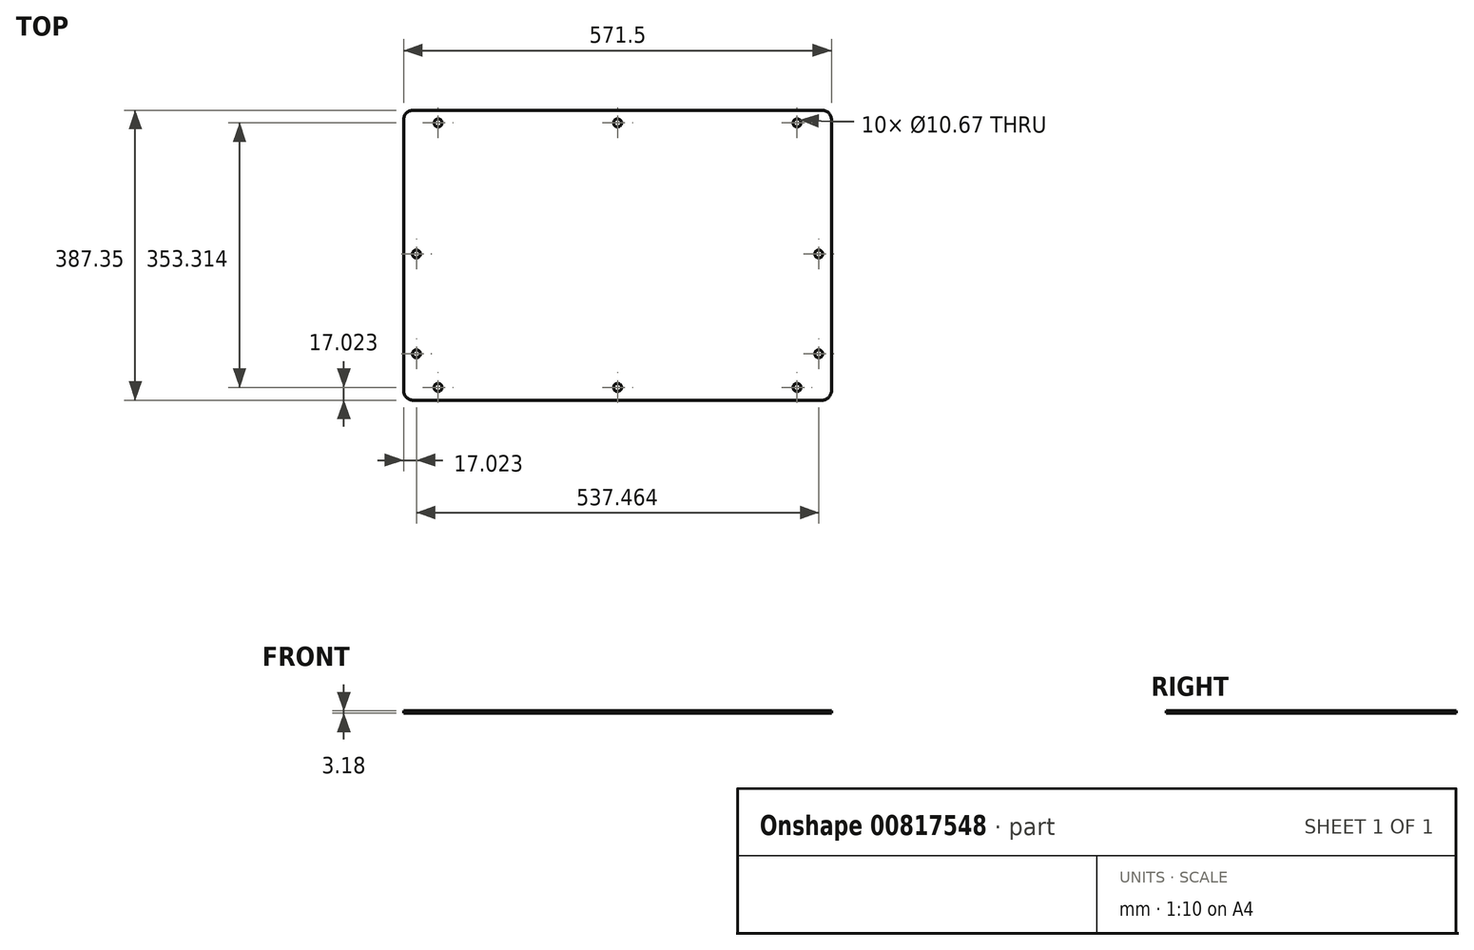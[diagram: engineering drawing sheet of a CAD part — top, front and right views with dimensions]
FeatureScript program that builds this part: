
annotation { "Feature Type Name" : "Feature", "Feature Type Description" : "" }
export const myFeature = defineFeature(function(context is Context, id is Id, definition is map)
    precondition{}
    {
        {
            var Q0;
            Q0=qCreatedBy(makeId("Top.planeOp"),FACE);
            var sketch = newSketch(context, id + "F0", { "sketchPlane" : qUnion([Q0])});
            skLineSegment(sketch, "E0.bottom", {"start": v(-512.78, 325.42) * mm, "end": v(33.32, 325.42) * mm});
            skLineSegment(sketch, "E0.top", {"start": v(-512.78, -61.93) * mm, "end": v(33.32, -61.93) * mm});
            skLineSegment(sketch, "E0.left", {"start": v(-525.48, 312.72) * mm, "end": v(-525.48, -49.23) * mm});
            skLineSegment(sketch, "E0.right", {"start": v(46.02, 312.72) * mm, "end": v(46.02, -49.23) * mm});
            skPoint(sketch, "E1.visualSharp", {"position": v(-525.48, 325.42) * mm});
            skArc(sketch, "E1.filletArc", {"start": v(-512.78, 325.42) * mm, "mid": v(-521.76, 321.7) * mm, "end": v(-525.48, 312.72) * mm});
            skPoint(sketch, "E2.visualSharp", {"position": v(-525.48, -61.93) * mm});
            skArc(sketch, "E2.filletArc", {"start": v(-525.48, -49.23) * mm, "mid": v(-521.76, -58.2) * mm, "end": v(-512.78, -61.93) * mm});
            skPoint(sketch, "E3.visualSharp", {"position": v(46.02, -61.93) * mm});
            skArc(sketch, "E3.filletArc", {"start": v(33.32, -61.93) * mm, "mid": v(42.3, -58.2) * mm, "end": v(46.02, -49.23) * mm});
            skPoint(sketch, "E4.visualSharp", {"position": v(46.02, 325.42) * mm});
            skArc(sketch, "E4.filletArc", {"start": v(46.02, 312.72) * mm, "mid": v(42.3, 321.7) * mm, "end": v(33.32, 325.42) * mm});
            skCircle(sketch, "E5", {"center": v(-479.44, 308.4) * mm, "radius": 5.33 * mm});
            skCircle(sketch, "E6", {"center": v(-239.73, 308.4) * mm, "radius": 5.33 * mm});
            skCircle(sketch, "E7", {"center": v(29, 133.35) * mm, "radius": 5.33 * mm});
            skCircle(sketch, "E8", {"center": v(29, 0) * mm, "radius": 5.33 * mm});
            skCircle(sketch, "E9", {"center": v(0, -44.9) * mm, "radius": 5.33 * mm});
            skCircle(sketch, "E10", {"center": v(-239.73, -44.9) * mm, "radius": 5.33 * mm});
            skCircle(sketch, "E11", {"center": v(-508.46, 0) * mm, "radius": 5.33 * mm});
            skCircle(sketch, "E12", {"center": v(-508.46, 133.35) * mm, "radius": 5.33 * mm});
            skCircle(sketch, "E13", {"center": v(-479.45, -44.9) * mm, "radius": 5.33 * mm});
            skCircle(sketch, "E14", {"center": v(0, 308.4) * mm, "radius": 5.33 * mm});
            skSolve(sketch);
        }
        {
            var Q0;
            Q0 = qSketchRegion(id + "F0", true);
            extrude(context, id + "F1", {"entities" : qUnion([Q0]), "depth" : 3.17 * mm, "offsetDistance" : 25.4 * mm});
        }
    });
